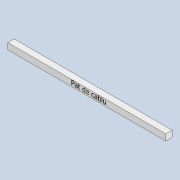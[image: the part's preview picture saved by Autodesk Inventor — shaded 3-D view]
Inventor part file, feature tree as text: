
AUTODESK INVENTOR PART (.ipt)
format: ipt  version: 2020 (Build 240168000, 168)  size: 78,848 bytes
history: native  units: mm
features: sketch x2, extrude x1
ambient origin geometry x8: Origin, YZ Plane, XZ Plane, XY Plane, X Axis, Y Axis, Z Axis, Center Point
bodies: Solid1 (feature_tree)
feature tree (3):
  extrude  "Extrusion1"  Depth=500.0mm
  sketch  "Sketch2"  dims[d2=20.0mm d3=0.0mm]
  sketch  "Sketch1"  dims[d0=20.0mm d1=500.0mm]
